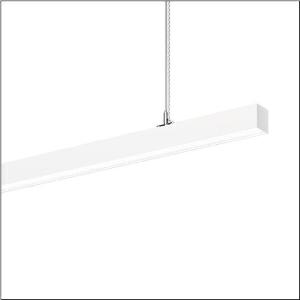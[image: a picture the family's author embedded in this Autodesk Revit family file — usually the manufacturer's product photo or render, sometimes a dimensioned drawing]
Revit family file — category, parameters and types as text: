
# Revit family: silica_r__21_51mx33dc3dwb_1062
name_source: partatom
category: Lighting Fixtures
units: mm (PartAtom-declared; Revit-internal decimal feet)

## family parameters
Cut with Voids When Loaded = No
Host = Face
Light Source = No
Part Type = Normal
Room Calculation Point = No
Round Connector Dimension = Use Diameter
Shared = No

## types (1)
- --- (1 x LED, 14780 lm, 99.5 W, 3000K)
    Apparent Load = 100 VA
    CIE Flux Codes = 78 96 99 55 100
    Color Rendering = 80
    Color Temperature = 3000K
    Default Elevation = 1800 mm
    Description = Silica® 21, office luminaire, primary optical cover: prismatic diffuser, of PMMA, CAT 2 (L<= 3000cd/m²), light emission: direct/indirect distribution, primary light characteristic: symmetric, installation type: suspended mounting, LED, rated luminous flux: 14.780lm, luminous efficacy: 149lm/W, light colour: 830, colour temperature: 3000K, with terminal, 3+2-pole, max. 2.5mm², mains connection: 220..240V, AC, 50/60Hz, rated input power: 99.5W, luminaire housing, of aluminium, traffic white (RAL 9016), length: 3.004mm, width: 53mm, height: 53mm, protection rating (complete): IP20, insulation class (complete): insulation class I (protective earthing), certification: CE, permissible operating ambient temperature: 0..+35°C, standard: EN 50419, packaging unit: 1 piece
    Height = 53 mm
    Lamp = 1 x LED
    Lamp Light Flux = 14780 lm
    Lamp Power = 99.5 W
    Lamp count = 1
    Length = 3004 mm
    Luminous efficacy = 149 lm/W
    Manufacturer = Siteco
    ModVariant = No
    Model = 51MX33DC3DWB
    Mounting Place = Ceiling
    Mounting Type = Pendant
    Number of Poles = 1
    OnlyDefault = Yes
    Power Factor = 1
    Product Name = Silica® 21
    Product group = office luminaire | ceiling pendant
    ProductGroupID = 902
    Protection Class = Protection class I
    Protection Degree = IP 20
    RLX_Detail_Level = 1
    RLX_Emergency_Light_Flux = 0 lm
    RLX_Emergency_Type = 0
    RLX_Emergency_Type_DB = No
    RlxData = <blob elided: 21425 chars, md5=14954933>
    Socket = socket
    Standby Power = 0 W
    System Light Flux = 14780 lm
    System Power = 100 W
    Type Comments = factory setting: luminous flux: 100 % | dim-lin: 254 | 345 mA
    Type Image = l_1297784.jpg
    URL = http://relux.com
    VarID = @adj_049153
    Voltage = 0 V
    Weight = 0.00 kg
    Width = 53 mm

## geometry (parser evidence)
native form markers: Blend x4, Sweep x15
no freeform markers — native parametric forms only
